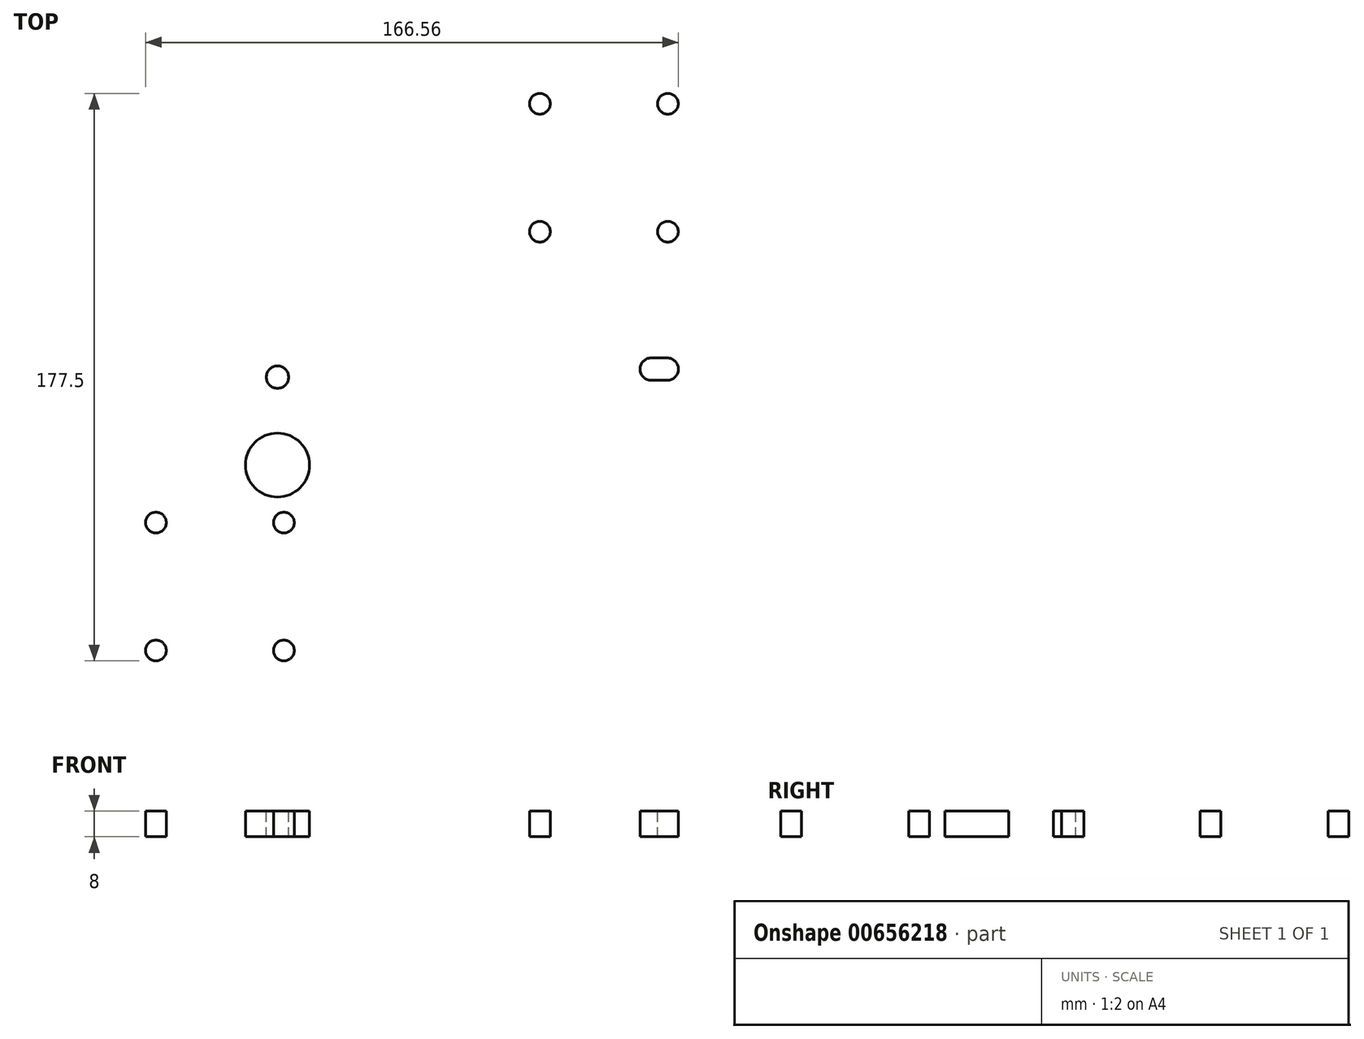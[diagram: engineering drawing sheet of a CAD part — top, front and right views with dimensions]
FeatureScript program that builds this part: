
annotation { "Feature Type Name" : "Feature", "Feature Type Description" : "" }
export const myFeature = defineFeature(function(context is Context, id is Id, definition is map)
    precondition{}
    {
        {
            var Q0;
            Q0=qCreatedBy(makeId("Top.planeOp"),FACE);
            var sketch = newSketch(context, id + "F0", { "sketchPlane" : qUnion([Q0])});
            skLineSegment(sketch, "E0.bottom", {"start": v(-87.5, 92.5) * mm, "end": v(87.5, 92.5) * mm});
            skLineSegment(sketch, "E0.top", {"start": v(-87.5, -92.5) * mm, "end": v(87.5, -92.5) * mm});
            skLineSegment(sketch, "E0.left", {"start": v(-87.5, 92.5) * mm, "end": v(-87.5, -92.5) * mm});
            skLineSegment(sketch, "E0.right", {"start": v(87.5, 92.5) * mm, "end": v(87.5, -92.5) * mm});
            skSolve(sketch);
        }
        {
            var Q0;
            Q0=makeQuery(id+"F0.imprint","IMPRINT",FACE,{"disambiguationData":[TD([[makeQuery(id+"F0.imprint","IMPRINT",EDGE,{"derivedFrom":sQuery(id+"F0.wireOp",EDGE,"E0.bottom")}),-1.0]])]});
            extrude(context, id + "F1", {"entities" : qUnion([Q0]), "oppositeDirection" : true, "depth" : 8 * mm, "offsetDistance" : 25 * mm});
        }
        {
            var Q0;
            Q0=makeQuery(id+"F1.opExtrude","CAP_FACE",FACE,{"disambiguationData":[OSD([sQuery(id+"F0.wireOp",EDGE,"E0.bottom"),sQuery(id+"F0.wireOp",EDGE,"E0.top"),sQuery(id+"F0.wireOp",EDGE,"E0.left"),sQuery(id+"F0.wireOp",EDGE,"E0.right")])],"isStart":true});
            var sketch = newSketch(context, id + "F2", { "sketchPlane" : qUnion([Q0])});
            skCircle(sketch, "E1", {"center": v(40, -85.5) * mm, "radius": 3.25 * mm});
            skCircle(sketch, "E2", {"center": v(80, -85.5) * mm, "radius": 3.25 * mm});
            skCircle(sketch, "E3", {"center": v(42, -27.5) * mm, "radius": 10 * mm});
            skCircle(sketch, "E4", {"center": v(40, -45.5) * mm, "radius": 3.25 * mm});
            skCircle(sketch, "E5", {"center": v(80, -45.5) * mm, "radius": 3.25 * mm});
            skCircle(sketch, "E6", {"center": v(0, -42.5) * mm, "radius": 20 * mm});
            skCircle(sketch, "E7.MirrorC", {"center": v(40, 85.5) * mm, "radius": 3.25 * mm});
            skCircle(sketch, "E8.MirrorC", {"center": v(80, 85.5) * mm, "radius": 3.25 * mm});
            skCircle(sketch, "E9.MirrorC", {"center": v(40, 45.5) * mm, "radius": 3.25 * mm});
            skCircle(sketch, "E10.MirrorC", {"center": v(80, 45.5) * mm, "radius": 3.25 * mm});
            skCircle(sketch, "E11.MirrorC", {"center": v(-80, 85.5) * mm, "radius": 3.25 * mm});
            skCircle(sketch, "E12.MirrorC", {"center": v(-80, 45.5) * mm, "radius": 3.25 * mm});
            skCircle(sketch, "E13.MirrorC", {"center": v(-40, 45.5) * mm, "radius": 3.25 * mm});
            skCircle(sketch, "E14.MirrorC", {"center": v(-40, 85.5) * mm, "radius": 3.25 * mm});
            skCircle(sketch, "E15.MirrorC", {"center": v(-40, -85.5) * mm, "radius": 3.25 * mm});
            skCircle(sketch, "E16.MirrorC", {"center": v(-40, -45.5) * mm, "radius": 3.25 * mm});
            skCircle(sketch, "E17.MirrorC", {"center": v(-80, -45.5) * mm, "radius": 3.25 * mm});
            skCircle(sketch, "E18.MirrorC", {"center": v(-80, -85.5) * mm, "radius": 3.25 * mm});
            skCircle(sketch, "E19.MirrorC", {"center": v(-42, -27.5) * mm, "radius": 10 * mm});
            skCircle(sketch, "E20", {"center": v(42, 0) * mm, "radius": 3.5 * mm});
            skCircle(sketch, "E21.MirrorC", {"center": v(-42, 0) * mm, "radius": 3.5 * mm});
            skArc(sketch, "E22", {"start": v(79.81, 29) * mm, "mid": v(83.31, 32.5) * mm, "end": v(79.81, 36) * mm});
            skLineSegment(sketch, "E23", {"start": v(74.81, 29) * mm, "end": v(79.81, 29) * mm});
            skLineSegment(sketch, "E24", {"start": v(77.31, 29) * mm, "end": v(77.31, 24.51) * mm});
            skLineSegment(sketch, "E25.MirrorCS", {"start": v(74.81, 36) * mm, "end": v(79.81, 36) * mm});
            skArc(sketch, "E26", {"start": v(74.81, 36) * mm, "mid": v(71.31, 32.5) * mm, "end": v(74.81, 29) * mm});
            skArc(sketch, "E27.MirrorCS", {"start": v(79.81, 6) * mm, "mid": v(83.31, 2.5) * mm, "end": v(79.81, -1) * mm});
            skLineSegment(sketch, "E28.MirrorCS", {"start": v(74.81, -1) * mm, "end": v(79.81, -1) * mm});
            skLineSegment(sketch, "E29.MirrorCS", {"start": v(74.81, 6) * mm, "end": v(79.81, 6) * mm});
            skArc(sketch, "E30.MirrorCS", {"start": v(74.81, -1) * mm, "mid": v(71.31, 2.5) * mm, "end": v(74.81, 6) * mm});
            skCircle(sketch, "E31", {"center": v(67.5, -75) * mm, "radius": 3 * mm});
            skCircle(sketch, "E32.MirrorC", {"center": v(-67.5, -75) * mm, "radius": 3 * mm});
            skSolve(sketch);
        }
        {
            var Q0;
            Q0=makeQuery(id+"F2.imprint","IMPRINT",FACE,{"disambiguationData":[TD([[makeQuery(id+"F2.imprint","IMPRINT",EDGE,{"derivedFrom":sQuery(id+"F2.wireOp",EDGE,"E11.MirrorC")}),1.0]])]});
            var Q1;
            Q1=makeQuery(id+"F2.imprint","IMPRINT",FACE,{"disambiguationData":[TD([[makeQuery(id+"F2.imprint","IMPRINT",EDGE,{"derivedFrom":sQuery(id+"F2.wireOp",EDGE,"E14.MirrorC")}),1.0]])]});
            var Q2;
            Q2=makeQuery(id+"F2.imprint","IMPRINT",FACE,{"disambiguationData":[TD([[makeQuery(id+"F2.imprint","IMPRINT",EDGE,{"derivedFrom":sQuery(id+"F2.wireOp",EDGE,"E13.MirrorC")}),1.0]])]});
            var Q3;
            Q3=makeQuery(id+"F2.imprint","IMPRINT",FACE,{"disambiguationData":[TD([[makeQuery(id+"F2.imprint","IMPRINT",EDGE,{"derivedFrom":sQuery(id+"F2.wireOp",EDGE,"E12.MirrorC")}),1.0]])]});
            var Q4;
            Q4=makeQuery(id+"F2.imprint","IMPRINT",FACE,{"disambiguationData":[TD([[makeQuery(id+"F2.imprint","IMPRINT",EDGE,{"derivedFrom":sQuery(id+"F2.wireOp",EDGE,"E7.MirrorC")}),-1.0]])]});
            var Q5;
            Q5=makeQuery(id+"F2.imprint","IMPRINT",FACE,{"disambiguationData":[TD([[makeQuery(id+"F2.imprint","IMPRINT",EDGE,{"derivedFrom":sQuery(id+"F2.wireOp",EDGE,"E8.MirrorC")}),-1.0]])]});
            var Q6;
            Q6=makeQuery(id+"F2.imprint","IMPRINT",FACE,{"disambiguationData":[TD([[makeQuery(id+"F2.imprint","IMPRINT",EDGE,{"derivedFrom":sQuery(id+"F2.wireOp",EDGE,"E9.MirrorC")}),-1.0]])]});
            var Q7;
            Q7=makeQuery(id+"F2.imprint","IMPRINT",FACE,{"disambiguationData":[TD([[makeQuery(id+"F2.imprint","IMPRINT",EDGE,{"derivedFrom":sQuery(id+"F2.wireOp",EDGE,"E10.MirrorC")}),-1.0]])]});
            var Q8;
            {var subQ1=sQuery(id+"F2.wireOp",EDGE,"E22");Q8=makeQuery(id+"F2.imprint","IMPRINT",FACE,{"disambiguationData":[TD([[makeQuery(id+"F2.imprint","IMPRINT",EDGE,{"derivedFrom":subQ1}),1.0]])]});}
            var Q9;
            Q9=makeQuery(id+"F2.imprint","IMPRINT",FACE,{"disambiguationData":[TD([[makeQuery(id+"F2.imprint","IMPRINT",EDGE,{"derivedFrom":sQuery(id+"F2.wireOp",EDGE,"E27.MirrorCS")}),-1.0]])]});
            var Q10;
            Q10=makeQuery(id+"F2.imprint","IMPRINT",FACE,{"disambiguationData":[TD([[makeQuery(id+"F2.imprint","IMPRINT",EDGE,{"derivedFrom":sQuery(id+"F2.wireOp",EDGE,"E20")}),1.0]])]});
            var Q11;
            Q11=makeQuery(id+"F2.imprint","IMPRINT",FACE,{"disambiguationData":[TD([[makeQuery(id+"F2.imprint","IMPRINT",EDGE,{"derivedFrom":sQuery(id+"F2.wireOp",EDGE,"E3")}),1.0]])]});
            var Q12;
            Q12=makeQuery(id+"F2.imprint","IMPRINT",FACE,{"disambiguationData":[TD([[makeQuery(id+"F2.imprint","IMPRINT",EDGE,{"derivedFrom":sQuery(id+"F2.wireOp",EDGE,"E4")}),1.0]])]});
            var Q13;
            Q13=makeQuery(id+"F2.imprint","IMPRINT",FACE,{"disambiguationData":[TD([[makeQuery(id+"F2.imprint","IMPRINT",EDGE,{"derivedFrom":sQuery(id+"F2.wireOp",EDGE,"E2")}),1.0]])]});
            var Q14;
            Q14=makeQuery(id+"F2.imprint","IMPRINT",FACE,{"disambiguationData":[TD([[makeQuery(id+"F2.imprint","IMPRINT",EDGE,{"derivedFrom":sQuery(id+"F2.wireOp",EDGE,"E5")}),1.0]])]});
            var Q15;
            Q15=makeQuery(id+"F2.imprint","IMPRINT",FACE,{"disambiguationData":[TD([[makeQuery(id+"F2.imprint","IMPRINT",EDGE,{"derivedFrom":sQuery(id+"F2.wireOp",EDGE,"E1")}),1.0]])]});
            var Q16;
            Q16=makeQuery(id+"F2.imprint","IMPRINT",FACE,{"disambiguationData":[TD([[makeQuery(id+"F2.imprint","IMPRINT",EDGE,{"derivedFrom":sQuery(id+"F2.wireOp",EDGE,"E15.MirrorC")}),-1.0]])]});
            var Q17;
            Q17=makeQuery(id+"F2.imprint","IMPRINT",FACE,{"disambiguationData":[TD([[makeQuery(id+"F2.imprint","IMPRINT",EDGE,{"derivedFrom":sQuery(id+"F2.wireOp",EDGE,"E18.MirrorC")}),-1.0]])]});
            var Q18;
            Q18=makeQuery(id+"F2.imprint","IMPRINT",FACE,{"disambiguationData":[TD([[makeQuery(id+"F2.imprint","IMPRINT",EDGE,{"derivedFrom":sQuery(id+"F2.wireOp",EDGE,"E17.MirrorC")}),-1.0]])]});
            var Q19;
            Q19=makeQuery(id+"F2.imprint","IMPRINT",FACE,{"disambiguationData":[TD([[makeQuery(id+"F2.imprint","IMPRINT",EDGE,{"derivedFrom":sQuery(id+"F2.wireOp",EDGE,"E16.MirrorC")}),-1.0]])]});
            var Q20;
            Q20=makeQuery(id+"F2.imprint","IMPRINT",FACE,{"disambiguationData":[TD([[makeQuery(id+"F2.imprint","IMPRINT",EDGE,{"derivedFrom":sQuery(id+"F2.wireOp",EDGE,"E19.MirrorC")}),-1.0]])]});
            var Q21;
            Q21=makeQuery(id+"F2.imprint","IMPRINT",FACE,{"disambiguationData":[TD([[makeQuery(id+"F2.imprint","IMPRINT",EDGE,{"derivedFrom":sQuery(id+"F2.wireOp",EDGE,"E21.MirrorC")}),-1.0]])]});
            var Q22;
            Q22=makeQuery(id+"F2.imprint","IMPRINT",FACE,{"disambiguationData":[TD([[makeQuery(id+"F2.imprint","IMPRINT",EDGE,{"derivedFrom":sQuery(id+"F2.wireOp",EDGE,"E6")}),1.0]])]});
            extrude(context, id + "F3", {"entities" : qUnion([Q0, Q1, Q2, Q3, Q4, Q5, Q6, Q7, Q8, Q9, Q10, Q11, Q12, Q13, Q14, Q15, Q16, Q17, Q18, Q19, Q20, Q21, Q22]), "operationType" : NewBodyOperationType.REMOVE, "oppositeDirection" : true, "depth" : 25 * mm, "offsetDistance" : 25 * mm});
        }
        {
            var Q0;
            Q0=makeQuery(id+"F1.opExtrude","CAP_FACE",FACE,{"disambiguationData":[OSD([sQuery(id+"F0.wireOp",EDGE,"E0.bottom"),sQuery(id+"F0.wireOp",EDGE,"E0.top"),sQuery(id+"F0.wireOp",EDGE,"E0.left"),sQuery(id+"F0.wireOp",EDGE,"E0.right")])],"isStart":false});
            var sketch = newSketch(context, id + "F4", { "sketchPlane" : qUnion([Q0])});
            skCircle(sketch, "E33", {"center": v(-67.5, 75) * mm, "radius": 3 * mm});
            skCircle(sketch, "E34.MirrorC", {"center": v(67.5, 75) * mm, "radius": 3 * mm});
            skSolve(sketch);
        }
        {
            var Q0;
            Q0=sQuery(id+"F4.wireOp",VERTEX,"E33.center");
            var Q1;
            Q1=sQuery(id+"F4.wireOp",VERTEX,"E34.MirrorC.center");
            var Q2;
            Q2=makeQuery(id+"F1.opExtrude","SWEPT_BODY",BODY,{"disambiguationData":[OSD([sQuery(id+"F0.wireOp",EDGE,"E0.bottom"),sQuery(id+"F0.wireOp",EDGE,"E0.top"),sQuery(id+"F0.wireOp",EDGE,"E0.left"),sQuery(id+"F0.wireOp",EDGE,"E0.right")])]});
            hole(context, id + "F5", {"style" : HoleStyle.C_BORE, "endStyle" : HoleEndStyle.BLIND, "holeDiameter" : 6 * mm, "cBoreDiameter" : 10 * mm, "cBoreDepth" : 5 * mm, "majorDiameter" : 5 * mm, "holeDepth" : 15 * mm, "isTappedThrough" : true, "tappedDepth" : 12 * mm, "tapClearance" : 3, "locations" : qUnion([Q0, Q1]), "scope" : qUnion([Q2])});
        }
    });
